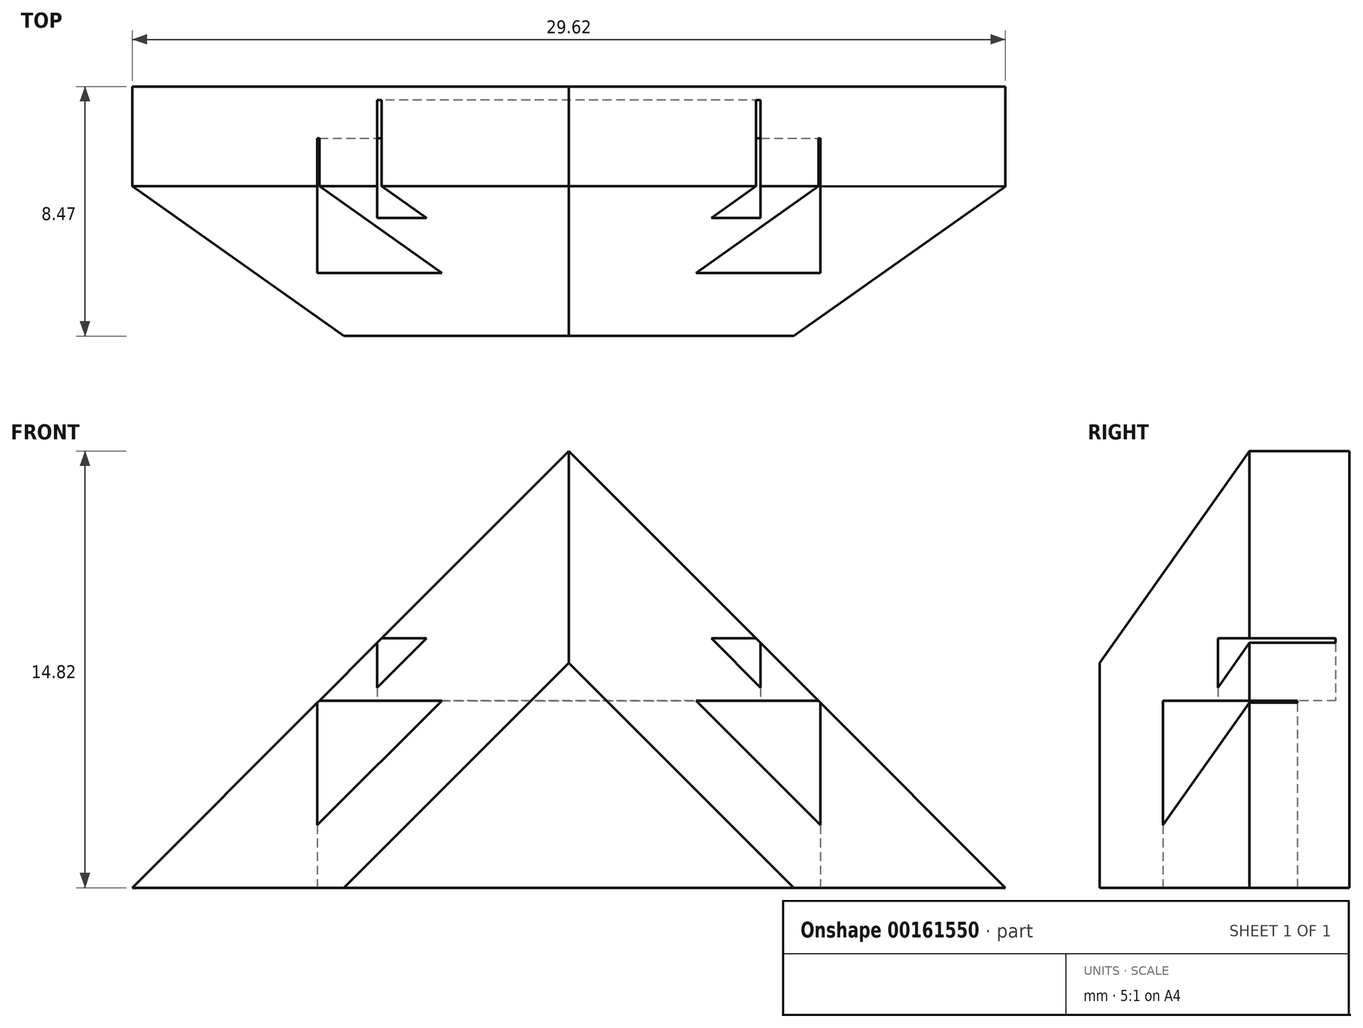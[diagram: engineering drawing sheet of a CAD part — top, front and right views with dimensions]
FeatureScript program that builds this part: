
annotation { "Feature Type Name" : "Feature", "Feature Type Description" : "" }
export const myFeature = defineFeature(function(context is Context, id is Id, definition is map)
    precondition{}
    {
        {
            var Q0;
            Q0=qCreatedBy(makeId("Front.planeOp"),FACE);
            var sketch = newSketch(context, id + "F0", { "sketchPlane" : qUnion([Q0])});
            skLineSegment(sketch, "E0.top", {"start": v(-5.67, 12.48) * mm, "end": v(7.03, 12.48) * mm});
            skLineSegment(sketch, "E1", {"start": v(-5.67, 20.95) * mm, "end": v(0.68, 27.3) * mm});
            skLineSegment(sketch, "E2", {"start": v(0.68, 27.3) * mm, "end": v(7.03, 20.95) * mm});
            skLineSegment(sketch, "E3", {"start": v(-5.67, 20.95) * mm, "end": v(-14.14, 12.48) * mm});
            skLineSegment(sketch, "E4", {"start": v(7.03, 20.95) * mm, "end": v(15.48, 12.48) * mm});
            skLineSegment(sketch, "E5", {"start": v(-14.14, 12.48) * mm, "end": v(-5.67, 12.48) * mm});
            skLineSegment(sketch, "E6", {"start": v(7.03, 12.48) * mm, "end": v(15.48, 12.48) * mm});
            skSolve(sketch);
        }
        {
            var Q0;
            Q0=makeQuery(id+"F0.imprint","IMPRINT",FACE,{"disambiguationData":[TD([[makeQuery(id+"F0.imprint","IMPRINT",EDGE,{"derivedFrom":sQuery(id+"F0.wireOp",EDGE,"E0.top")}),1.0]])]});
            extrude(context, id + "F1", {"entities" : qUnion([Q0]), "depth" : 8.47 * mm});
        }
        {
            var Q0;
            Q0=makeQuery(id+"F1.opExtrude","CAP_EDGE",EDGE,{"disambiguationData":[OSD([sQuery(id+"F0.wireOp",EDGE,"E1"),sQuery(id+"F0.wireOp",EDGE,"E3")])],"isStart":false});
            chamfer(context, id + "F2", {"entities" : qUnion([Q0]), "width" : 5.08 * mm, "tangentPropagation" : true});
        }
        {
            var Q0;
            Q0=makeQuery(id+"F1.opExtrude","CAP_EDGE",EDGE,{"disambiguationData":[OSD([sQuery(id+"F0.wireOp",EDGE,"E2")])],"isStart":false});
            chamfer(context, id + "F3", {"entities" : qUnion([Q0]), "width" : 5.08 * mm, "tangentPropagation" : true});
        }
        {
            var Q0;
            Q0=makeQuery(id+"F1.opExtrude","SWEPT_FACE",FACE,{"disambiguationData":[OSD([sQuery(id+"F0.wireOp",EDGE,"E0.top"),sQuery(id+"F0.wireOp",EDGE,"E5"),sQuery(id+"F0.wireOp",EDGE,"E6")])]});
            var sketch = newSketch(context, id + "F4", { "sketchPlane" : qUnion([Q0])});
            skLineSegment(sketch, "E7.bottom", {"start": v(-7.86, 6.32) * mm, "end": v(9.21, 6.32) * mm});
            skLineSegment(sketch, "E7.top", {"start": v(-7.86, 1.76) * mm, "end": v(9.21, 1.76) * mm});
            skLineSegment(sketch, "E7.left", {"start": v(-7.86, 6.32) * mm, "end": v(-7.86, 1.76) * mm});
            skLineSegment(sketch, "E7.right", {"start": v(9.21, 6.32) * mm, "end": v(9.21, 1.76) * mm});
            skPoint(sketch, "E7.middle", {"position": v(0.68, 4.04) * mm});
            skPoint(sketch, "E7.middle.positionSnap0", {"position": v(0.68, 8.47) * mm});
            skPoint(sketch, "E7.centerSnap0", {"position": v(0.68, 8.47) * mm});
            skSolve(sketch);
        }
        {
            var Q0;
            Q0 = qSketchRegion(id + "F4", true);
            extrude(context, id + "F5", {"entities" : qUnion([Q0]), "operationType" : NewBodyOperationType.REMOVE, "oppositeDirection" : true, "depth" : 6.35 * mm});
        }
        {
            var Q0;
            Q0=makeQuery(id+"F5.boolean.opBoolean","COPY",FACE,{"derivedFrom":makeQuery(id+"F5.opExtrude","SWEPT_FACE",FACE,{"disambiguationData":[OSD([sQuery(id+"F4.wireOp",EDGE,"E7.top")])]})});
            extrude(context, id + "F6", {"entities" : qUnion([Q0]), "operationType" : NewBodyOperationType.REMOVE, "oppositeDirection" : true, "depth" : 1 / 609.6 * mm});
        }
        {
            var Q0;
            {var subQ0=sQuery(id+"F4.wireOp",EDGE,"E7.top");Q0=makeQuery(id+"F6.boolean.opBoolean","MERGE",FACE,{"derivedFrom":[makeQuery(id+"F5.boolean.opBoolean","COPY",FACE,{"derivedFrom":makeQuery(id+"F5.opExtrude","CAP_FACE",FACE,{"disambiguationData":[OSD([sQuery(id+"F4.wireOp",EDGE,"E7.bottom"),subQ0,sQuery(id+"F4.wireOp",EDGE,"E7.left"),sQuery(id+"F4.wireOp",EDGE,"E7.right")])],"isStart":false})}),makeQuery(id+"F6.opExtrude","SWEPT_FACE",FACE,{"disambiguationData":[OSD([subQ0]),TDD([makeQuery(id+"F5.boolean.opBoolean","COPY",EDGE,{"derivedFrom":makeQuery(id+"F5.opExtrude","CAP_EDGE",EDGE,{"disambiguationData":[OSD([subQ0])],"isStart":false})})])]})]});}
            var sketch = newSketch(context, id + "F7", { "sketchPlane" : qUnion([Q0])});
            skLineSegment(sketch, "E8.bottom", {"start": v(7.18, 1.52) * mm, "end": v(-5.83, 1.52) * mm});
            skLineSegment(sketch, "E8.top", {"start": v(7.18, 4.46) * mm, "end": v(-5.83, 4.46) * mm});
            skLineSegment(sketch, "E8.left", {"start": v(7.18, 1.52) * mm, "end": v(7.18, 4.46) * mm});
            skLineSegment(sketch, "E8.right", {"start": v(-5.83, 1.52) * mm, "end": v(-5.83, 4.46) * mm});
            skPoint(sketch, "E8.middle", {"position": v(0.67, 3) * mm});
            skPoint(sketch, "E8.middle.positionSnap0", {"position": v(0.67, 0.7) * mm});
            skPoint(sketch, "E8.centerSnap0", {"position": v(0.67, 0.7) * mm});
            skSolve(sketch);
        }
        {
            var Q0;
            Q0 = qSketchRegion(id + "F7", true);
            extrude(context, id + "F8", {"entities" : qUnion([Q0]), "operationType" : NewBodyOperationType.REMOVE, "oppositeDirection" : true, "depth" : 2.12 * mm});
        }
        {
            var Q0;
            Q0=makeQuery(id+"F8.boolean.opBoolean","COPY",FACE,{"derivedFrom":makeQuery(id+"F8.opExtrude","SWEPT_FACE",FACE,{"disambiguationData":[OSD([sQuery(id+"F7.wireOp",EDGE,"E8.bottom")])]})});
            extrude(context, id + "F9", {"entities" : qUnion([Q0]), "operationType" : NewBodyOperationType.REMOVE, "oppositeDirection" : true, "depth" : 1.06 * mm});
        }
    });
